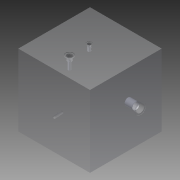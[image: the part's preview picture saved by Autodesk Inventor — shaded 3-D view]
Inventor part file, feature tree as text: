
AUTODESK INVENTOR PART (.ipt)
format: ipt  version: 2014 (Build 180170000, 170)  size: 264,704 bytes
history: native  units: mm
features: other x53, sketch x8, extrude x1
ambient origin geometry x8: Origin, YZ Plane, XZ Plane, XY Plane, X Axis, Y Axis, Z Axis, Center Point
bodies: 实体1 (feature_tree)
feature tree (62):
  other  "NULLNET"
  extrude  "拉伸1"  TaperAngle=0.0deg  [1 undecoded]
  other  "UCS1"
  other  "UCS2"
  other  "UCS3"
  other  "UCS4"
  other  "UCS5"
  other  "UCS6"
  other  "PLUG1"
  sketch  "草图1"  dims[d0=300.0mm d1=0.0mm]
  sketch  "草图3"  dims[d8=0.0mm d9=0.0mm d10=0.0mm d11=0.0mm d12=0.0mm d13=0.0mm]
  other  "曲面1"
  sketch  "草图5"  dims[d20=0.0mm d21=0.0mm d22=0.0mm d23=0.0mm d24=0.0mm d25=0.0mm]
  other  "曲面2"
  sketch  "草图8"  dims[d42=-9.96mm d43=0.13mm d44=0.0mm d45=0.0mm d49=-19.0mm d50=0.13mm d51=0.0mm d55=0.0mm d59=-16.0mm d60=0.13mm d61=0.0mm]
  other  "曲面3"
  other  "UCS1: YZ 平面"
  other  "UCS1: XZ 平面"
  other  "UCS1: XY 平面"
  other  "UCS1: X 轴"
  other  "UCS1: Y 轴"
  other  "UCS1: Z 轴"
  other  "UCS1: 原点"
  other  "UCS2: YZ 平面"
  other  "UCS2: XZ 平面"
  other  "UCS2: XY 平面"
  other  "UCS2: X 轴"
  other  "UCS2: Y 轴"
  other  "UCS2: Z 轴"
  other  "UCS2: 原点"
  other  "UCS3: YZ 平面"
  other  "UCS3: XZ 平面"
  other  "UCS3: XY 平面"
  other  "UCS3: X 轴"
  other  "UCS3: Y 轴"
  other  "UCS3: Z 轴"
  other  "UCS3: 原点"
  other  "UCS4: YZ 平面"
  other  "UCS4: XZ 平面"
  other  "UCS4: XY 平面"
  other  "UCS4: X 轴"
  other  "UCS4: Y 轴"
  other  "UCS4: Z 轴"
  other  "UCS4: 原点"
  other  "UCS5: YZ 平面"
  other  "UCS5: XZ 平面"
  other  "UCS5: XY 平面"
  other  "UCS5: X 轴"
  other  "UCS5: Y 轴"
  other  "UCS5: Z 轴"
  other  "UCS5: 原点"
  other  "UCS6: YZ 平面"
  other  "UCS6: XZ 平面"
  other  "UCS6: XY 平面"
  other  "UCS6: X 轴"
  other  "UCS6: Y 轴"
  other  "UCS6: Z 轴"
  other  "UCS6: 原点"
  sketch  "草图2"  dims[d2=0.0mm d3=0.0mm d4=0.0mm d5=0.0mm d6=0.0mm d7=0.0mm]
  sketch  "草图4"  dims[d14=0.0mm d15=0.0mm d16=0.0mm d17=0.0mm d18=0.0mm d19=0.0mm]
  sketch  "草图6"  dims[d26=0.0mm d27=0.0mm d28=0.0mm d29=0.0mm d30=0.0mm d31=0.0mm]
  sketch  "草图7"  dims[d32=0.0mm d33=0.0mm d34=0.0mm d35=0.0mm d36=0.0mm d37=0.0mm d38=0.0mm]
note: 1 required parameter value undecoded (feature->parameter linkage not recoverable at this tier; creation-order binding heuristic only, values carry confidence <= 0.55)
